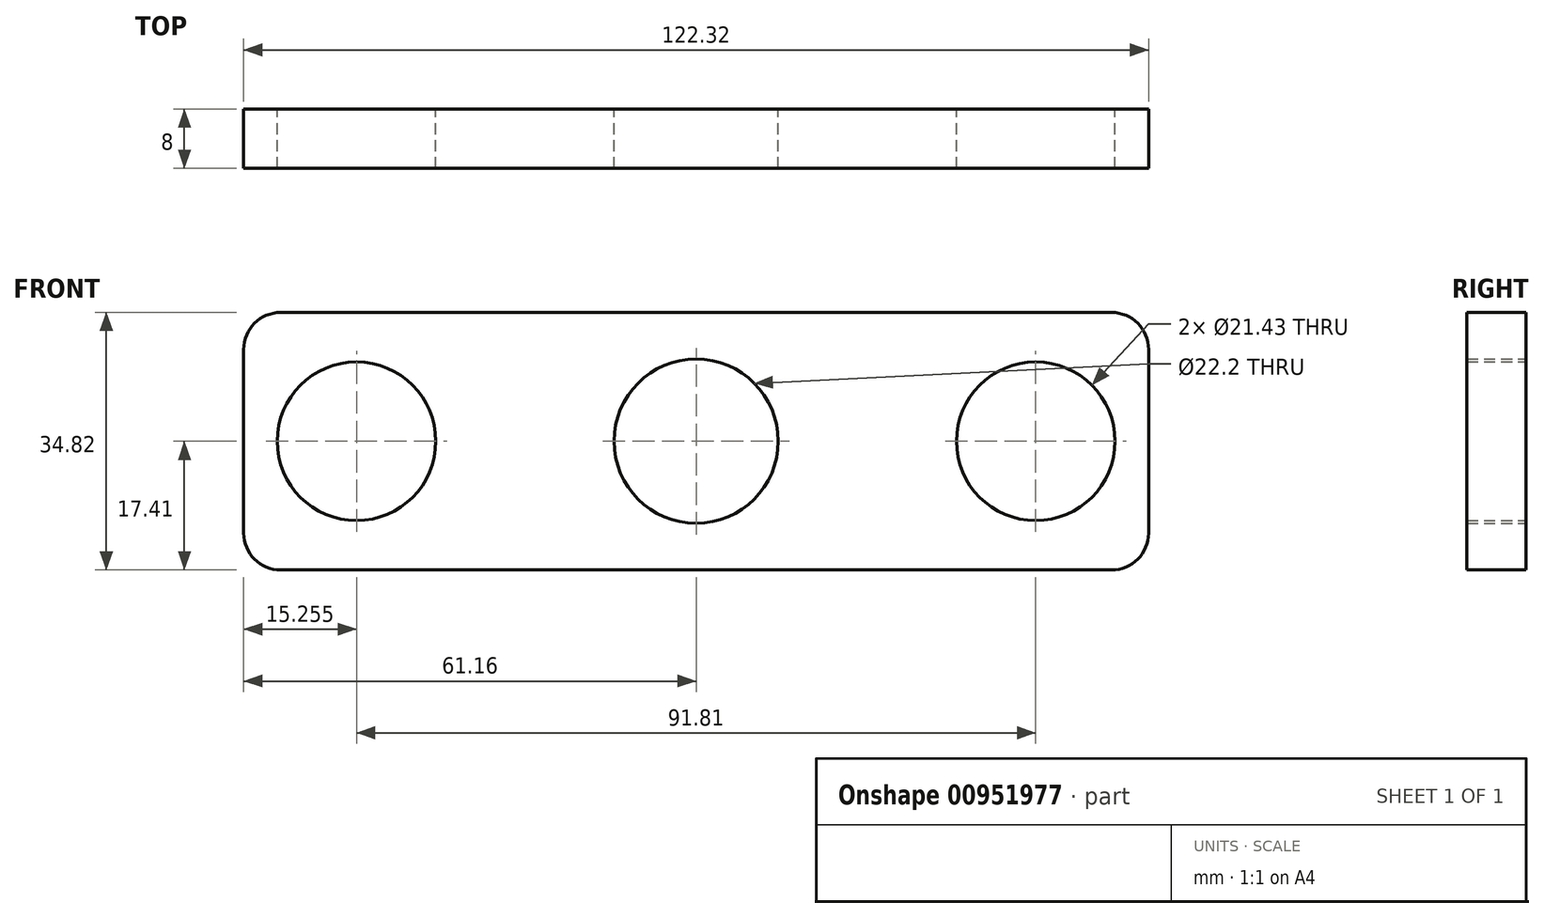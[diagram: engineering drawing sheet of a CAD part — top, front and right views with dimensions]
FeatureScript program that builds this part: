
annotation { "Feature Type Name" : "Feature", "Feature Type Description" : "" }
export const myFeature = defineFeature(function(context is Context, id is Id, definition is map)
    precondition{}
    {
        {
            var Q0;
            Q0=qCreatedBy(makeId("Front.planeOp"),FACE);
            var sketch = newSketch(context, id + "F0", { "sketchPlane" : qUnion([Q0])});
            skCircle(sketch, "E0", {"center": v(0, 0) * mm, "radius": 11.1 * mm});
            skLineSegment(sketch, "E1.bottom", {"start": v(-56.16, 17.41) * mm, "end": v(56.16, 17.41) * mm});
            skLineSegment(sketch, "E1.top", {"start": v(-56.16, -17.41) * mm, "end": v(56.16, -17.41) * mm});
            skLineSegment(sketch, "E1.left", {"start": v(-61.16, 12.41) * mm, "end": v(-61.16, -12.41) * mm});
            skLineSegment(sketch, "E1.right", {"start": v(61.16, 12.41) * mm, "end": v(61.16, -12.41) * mm});
            skPoint(sketch, "E2.visualSharp", {"position": v(-61.16, 17.41) * mm});
            skArc(sketch, "E2.filletArc", {"start": v(-56.16, 17.41) * mm, "mid": v(-59.7, 15.95) * mm, "end": v(-61.16, 12.41) * mm});
            skPoint(sketch, "E3.visualSharp", {"position": v(61.16, 17.41) * mm});
            skArc(sketch, "E3.filletArc", {"start": v(61.16, 12.41) * mm, "mid": v(59.7, 15.95) * mm, "end": v(56.16, 17.41) * mm});
            skPoint(sketch, "E4.visualSharp", {"position": v(61.16, -17.41) * mm});
            skArc(sketch, "E4.filletArc", {"start": v(56.16, -17.41) * mm, "mid": v(59.7, -15.95) * mm, "end": v(61.16, -12.41) * mm});
            skPoint(sketch, "E5.visualSharp", {"position": v(-61.16, -17.41) * mm});
            skArc(sketch, "E5.filletArc", {"start": v(-61.16, -12.41) * mm, "mid": v(-59.7, -15.95) * mm, "end": v(-56.16, -17.41) * mm});
            skCircle(sketch, "E6", {"center": v(-45.9, 0) * mm, "radius": 10.72 * mm});
            skCircle(sketch, "E7.MirrorC", {"center": v(45.9, 0) * mm, "radius": 10.72 * mm});
            skSolve(sketch);
        }
        {
            var Q0;
            Q0=makeQuery(id+"F0.imprint","IMPRINT",FACE,{"disambiguationData":[TD([[makeQuery(id+"F0.imprint","IMPRINT",EDGE,{"derivedFrom":sQuery(id+"F0.wireOp",EDGE,"E0")}),-1.0]])]});
            extrude(context, id + "F1", {"entities" : qUnion([Q0]), "depth" : 8 * mm, "offsetDistance" : 25 * mm});
        }
    });
